# Revit family: P200635WX-006c_WED560LHW
name_source: partatom
category: Specialty Equipment
units: mm (PartAtom-declared; Revit-internal decimal feet)

## family parameters
Always vertical = Yes
Cut with Voids When Loaded = No
Enable Cutting in Views = No
Maintain Annotation Orientation = No
Part Type = Normal
Room Calculation Point = No
Round Connector Dimension = Use Diameter
Shared = No
Work Plane-Based = No

## types (1)
- WED560LHW
    Accent Material = ARCAT - Plastic - Gray
    Amps = 0 A
    Back Panel Material = ARCAT - Metal - Aluminum
    Body Material = ARCAT - Metal - White
    Chrome Trim Material = ARCAT - Metal - Chrome
    Clearance Material = ARCAT - Clearance
    Default Elevation = 0"
    Depth = 31"
    Description = 7.4 cu.ft Front Load Long Vent Electric Dryer with Intuitive Controls
Sécheuse électrique avec commandes tactiles intuitives, 7.4 pi³
    Door Material = ARCAT - Metal - White
    Dsiplay Panel Material = ARCAT - Glass Tempered - Black
    Family Name = Electric Front-Load Dryer
    Feature 1 = Wrinkle Shield™ Option
Détection d'humidité perfectionnée
    Feature 2 = 7.4 cu. ft. Capacity
Wrinkle Shield™ Option
    Feature 3 = ENERGY STAR® Certified
Capacité de 7,4 pi³
    Glass Material = ARCAT - Glass Tempered - Clear
    Height = 38 3/4"
    Installation-Fabrication = https://www.whirlpool.com
https://www.whirlpool.com
    Leg Material = ARCAT - Plastic - White
    Manufacturer = Whirlpool
    Model = WED560LHW
    Voltage = 0 V
    Width = 27"

## geometry (parser evidence)
native form markers: Sweep x5
no freeform markers — native parametric forms only
